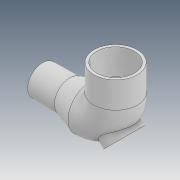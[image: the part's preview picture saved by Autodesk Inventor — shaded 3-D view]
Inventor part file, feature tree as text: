
AUTODESK INVENTOR PART (.ipt)
format: ipt  version: 2020 (Build 240168000, 168)  size: 205,312 bytes
history: native  units: mm
features: sketch x5, plane x4, revolve x3, extrude x1, projected_geometry x1
ambient origin geometry x8: Origin, YZ Plane, XZ Plane, XY Plane, X Axis, Y Axis, Z Axis, Center Point
bodies: Solid1 (feature_tree)
feature tree (14):
  revolve  "Revolution1"  [1 undecoded]
  plane  "Work Plane1"
  sketch  "Sketch2"  dims[d11=90.0deg d12=-20.0mm]
  revolve  "Revolution2"  [1 undecoded]
  plane  "Work Plane2"
  revolve  "Revolution3"  Angle=90.0deg
  plane  "Work Plane4"
  extrude  "Extrusion1"  Depth=15.0mm
  sketch  "Sketch1"  dims[d0=2.0mm d1=2.0mm d2=0.0mm d3=0.0mm d4=18.15mm d5=1.999932mm d6=14.0mm d7=0.0mm d8=1.85mm d9=2.122957mm d10=1.0mm]
  sketch  "Sketch3"  dims[d13=19.0mm d14=90.0deg]
  projected_geometry  "Projected Loop1"
  sketch  "Sketch4"  dims[d15=0.0mm d16=15.0mm]
  plane  "Work Plane3"
  sketch  "Sketch5"  dims[d17=20.0mm d18=11.0mm d19=11.25mm d20=1.2mm d21=1.2mm d22=90.0deg d23=135.0deg d24=36.0mm d25=25.0mm d26=10.0mm d27=0.0mm]
note: 2 required parameter values undecoded (feature->parameter linkage not recoverable at this tier; creation-order binding heuristic only, values carry confidence <= 0.55)
